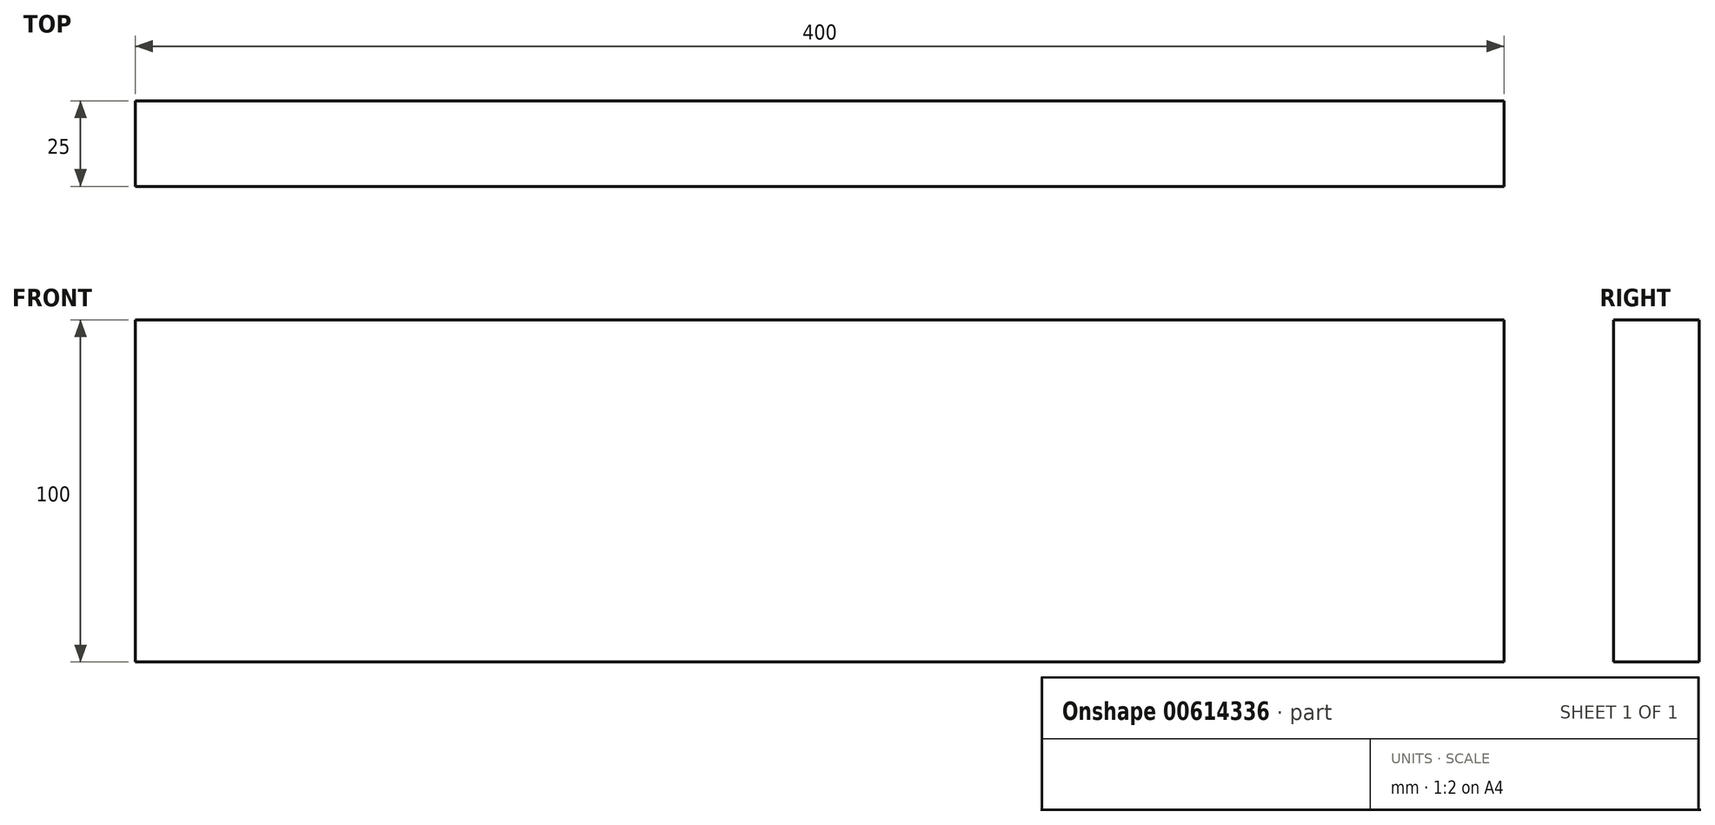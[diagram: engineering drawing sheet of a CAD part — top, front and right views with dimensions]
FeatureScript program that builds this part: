
annotation { "Feature Type Name" : "Feature", "Feature Type Description" : "" }
export const myFeature = defineFeature(function(context is Context, id is Id, definition is map)
    precondition{}
    {
        {
            var Q0;
            Q0=qCreatedBy(makeId("Front.planeOp"),FACE);
            var sketch = newSketch(context, id + "F0", { "sketchPlane" : qUnion([Q0])});
            skLineSegment(sketch, "E0.bottom", {"start": v(-184.02, -109.18) * mm, "end": v(-584.02, -109.18) * mm});
            skLineSegment(sketch, "E0.top", {"start": v(-184.02, -209.18) * mm, "end": v(-584.02, -209.18) * mm});
            skLineSegment(sketch, "E0.left", {"start": v(-184.02, -109.18) * mm, "end": v(-184.02, -209.18) * mm});
            skLineSegment(sketch, "E0.right", {"start": v(-584.02, -109.18) * mm, "end": v(-584.02, -209.18) * mm});
            skSolve(sketch);
        }
        {
            var Q0;
            Q0 = qSketchRegion(id + "F0", true);
            extrude(context, id + "F1", {"entities" : qUnion([Q0]), "depth" : 25 * mm, "offsetDistance" : 25 * mm});
        }
    });
